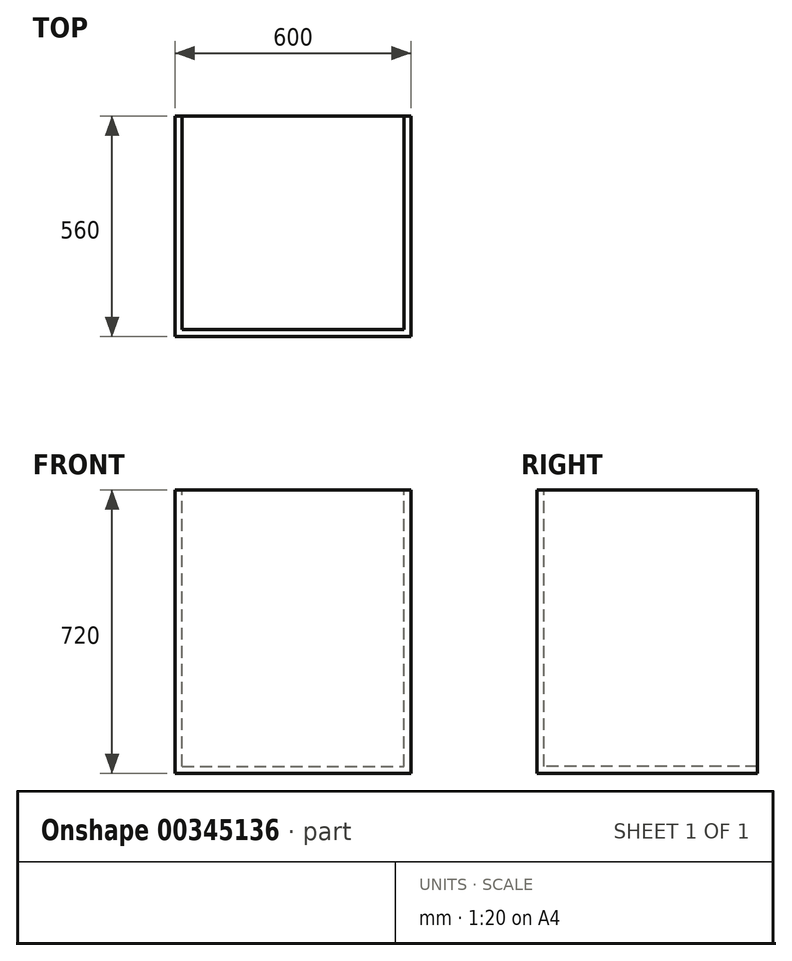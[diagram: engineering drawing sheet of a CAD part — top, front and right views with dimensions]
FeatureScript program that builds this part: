
annotation { "Feature Type Name" : "Feature", "Feature Type Description" : "" }
export const myFeature = defineFeature(function(context is Context, id is Id, definition is map)
    precondition{}
    {
        {
            var Q0;
            Q0=qCreatedBy(makeId("Front.planeOp"),FACE);
            var sketch = newSketch(context, id + "F0", { "sketchPlane" : qUnion([Q0])});
            skLineSegment(sketch, "E0.bottom", {"start": v(0, 0) * mm, "end": v(60.62, 0) * mm});
            skLineSegment(sketch, "E0.top", {"start": v(0, 48.44) * mm, "end": v(60.62, 48.44) * mm});
            skLineSegment(sketch, "E0.left", {"start": v(0, 0) * mm, "end": v(0, 48.44) * mm});
            skLineSegment(sketch, "E0.right", {"start": v(60.62, 0) * mm, "end": v(60.62, 48.44) * mm});
            skSolve(sketch);
        }
        {
            var Q0;
            Q0=makeQuery(id+"F0.imprint","IMPRINT",FACE,{"disambiguationData":[TD([[makeQuery(id+"F0.imprint","IMPRINT",EDGE,{"derivedFrom":sQuery(id+"F0.wireOp",EDGE,"E0.bottom")}),1.0]])]});
            extrude(context, id + "F1", {"entities" : qUnion([Q0]), "oppositeDirection" : true, "depth" : 560 * mm});
        }
        {
            var Q0;
            Q0=makeQuery(id+"F1.opExtrude","SWEPT_FACE",FACE,{"disambiguationData":[OSD([sQuery(id+"F0.wireOp",EDGE,"E0.left")])]});
            extrude(context, id + "F2", {"entities" : qUnion([Q0]), "operationType" : NewBodyOperationType.ADD, "oppositeDirection" : true, "depth" : 600 * mm});
        }
        {
            var Q0;
            {var subQ0=sQuery(id+"F0.wireOp",EDGE,"E0.bottom");Q0=makeQuery(id+"F2.boolean.opBoolean","MERGE",FACE,{"derivedFrom":[makeQuery(id+"F1.opExtrude","SWEPT_FACE",FACE,{"disambiguationData":[OSD([subQ0])]}),makeQuery(id+"F2.opExtrude","SWEPT_FACE",FACE,{"disambiguationData":[OSD([subQ0,sQuery(id+"F0.wireOp",EDGE,"E0.left")])]})]});}
            extrude(context, id + "F3", {"entities" : qUnion([Q0]), "operationType" : NewBodyOperationType.ADD, "oppositeDirection" : true, "depth" : 720 * mm});
        }
        {
            var Q0;
            {var subQ0=sQuery(id+"F0.wireOp",EDGE,"E0.left");var subQ1=sQuery(id+"F0.wireOp",EDGE,"E0.bottom");Q0=makeQuery(id+"F3.boolean.opBoolean","MERGE",FACE,{"derivedFrom":[makeQuery(id+"F2.boolean.opBoolean","MERGE",FACE,{"derivedFrom":[makeQuery(id+"F1.opExtrude","CAP_FACE",FACE,{"disambiguationData":[OSD([subQ1,sQuery(id+"F0.wireOp",EDGE,"E0.top"),subQ0,sQuery(id+"F0.wireOp",EDGE,"E0.right")])],"isStart":false}),makeQuery(id+"F2.opExtrude","SWEPT_FACE",FACE,{"disambiguationData":[OSD([subQ0]),TDD([makeQuery(id+"F1.opExtrude","CAP_EDGE",EDGE,{"disambiguationData":[OSD([subQ0])],"isStart":false})])]})]}),makeQuery(id+"F3.opExtrude","SWEPT_FACE",FACE,{"disambiguationData":[OSD([subQ1,subQ0]),TDD([makeQuery(id+"F2.boolean.opBoolean","MERGE",EDGE,{"derivedFrom":[makeQuery(id+"F1.opExtrude","CAP_EDGE",EDGE,{"disambiguationData":[OSD([subQ1])],"isStart":false}),makeQuery(id+"F2.opExtrude","SWEPT_EDGE",EDGE,{"disambiguationData":[OSD([subQ1,subQ0]),TDD([makeQuery(id+"F1.opExtrude","CAP_VERTEX",VERTEX,{"disambiguationData":[OSD([subQ1,subQ0])],"isStart":false})])]})]})])]})]});}
            var Q1;
            Q1=makeQuery(id+"F3.opExtrude","CAP_FACE",FACE,{"disambiguationData":[OSD([sQuery(id+"F0.wireOp",EDGE,"E0.bottom"),sQuery(id+"F0.wireOp",EDGE,"E0.left")])],"isStart":false});
            shell(context, id + "F4", {"entities" : qUnion([Q0, Q1]), "thickness" : 18 * mm});
        }
    });
